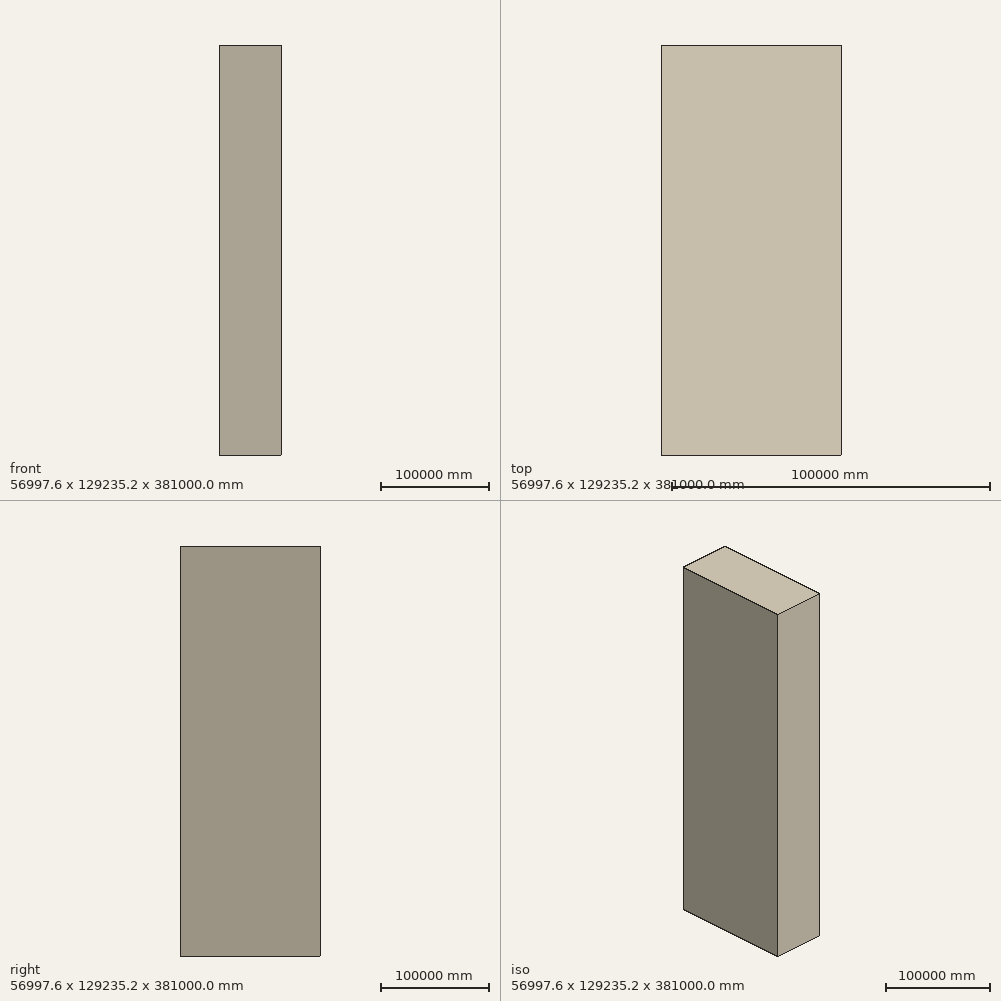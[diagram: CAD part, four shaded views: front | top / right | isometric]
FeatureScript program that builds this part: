
annotation { "Feature Type Name" : "Feature", "Feature Type Description" : "" }
export const myFeature = defineFeature(function(context is Context, id is Id, definition is map)
    precondition{}
    {
        {
            var Q0;
            Q0=qCreatedBy(makeId("Front.planeOp"),FACE);
            var sketch = newSketch(context, id + "F0", { "sketchPlane" : qUnion([Q0])});
            skLineSegment(sketch, "E0", {"start": v(0, 0) * mm, "end": v(-56997.6, 0) * mm});
            skLineSegment(sketch, "E1", {"start": v(0, 0) * mm, "end": v(0, 381000) * mm});
            skLineSegment(sketch, "E2", {"start": v(-56997.6, 0) * mm, "end": v(-56997.6, 381000) * mm});
            skLineSegment(sketch, "E3", {"start": v(-56997.6, 381000) * mm, "end": v(0, 381000) * mm});
            skLineSegment(sketch, "E4", {"start": v(-28498.8, 381000) * mm, "end": v(-28498.8, 443179.2) * mm});
            skSolve(sketch);
        }
        {
            var Q0;
            Q0=makeQuery(id+"F0.imprint","IMPRINT",FACE,{"disambiguationData":[TD([[makeQuery(id+"F0.imprint","IMPRINT",EDGE,{"derivedFrom":sQuery(id+"F0.wireOp",EDGE,"E0")}),-1.0]])]});
            extrude(context, id + "F1", {"entities" : qUnion([Q0]), "endBound" : BoundingType.SYMMETRIC, "depth" : 129235.2 * mm, "offsetDistance" : 30.48 * mm});
        }
        {
            var Q0;
            Q0=sQuery(id+"F0.wireOp",EDGE,"E4");
            extrude(context, id + "F2", {"bodyType" : ToolBodyType.SURFACE, "surfaceEntities" : qUnion([Q0]), "endBound" : BoundingType.SYMMETRIC, "depth" : 1524 * mm, "offsetDistance" : 30.48 * mm});
        }
    });
